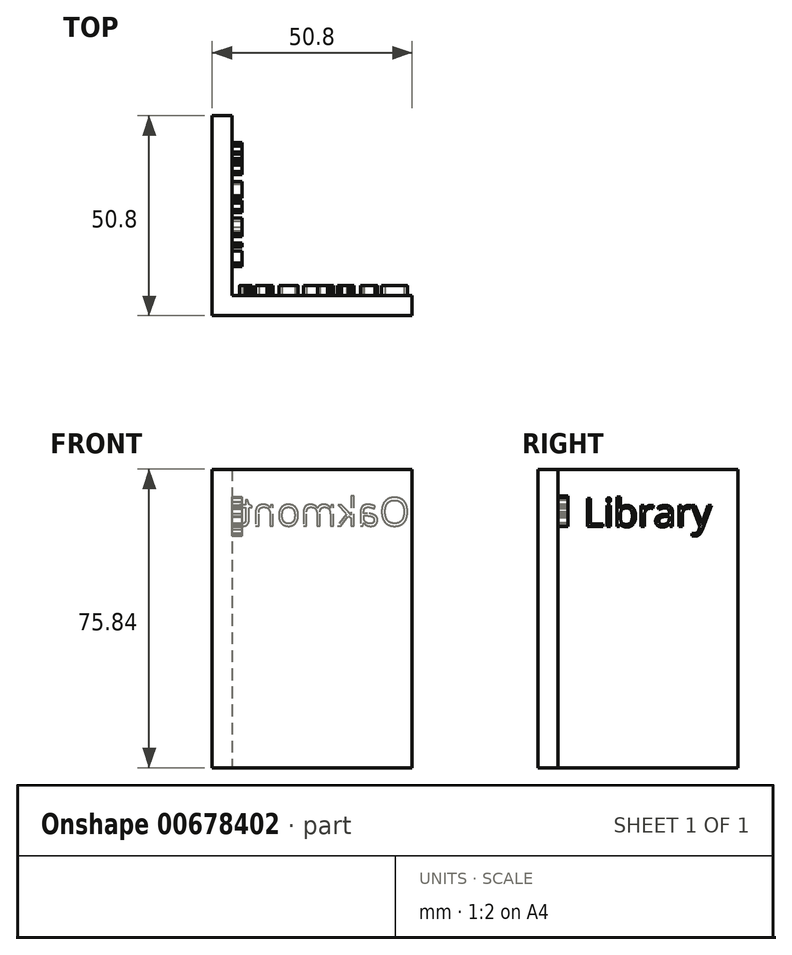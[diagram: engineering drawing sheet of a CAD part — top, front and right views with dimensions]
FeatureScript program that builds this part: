
annotation { "Feature Type Name" : "Feature", "Feature Type Description" : "" }
export const myFeature = defineFeature(function(context is Context, id is Id, definition is map)
    precondition{}
    {
        {
            var Q0;
            Q0=qCreatedBy(makeId("Right.planeOp"),FACE);
            var sketch = newSketch(context, id + "F0", { "sketchPlane" : qUnion([Q0])});
            skLineSegment(sketch, "E0.bottom", {"start": v(25.4, 37.92) * mm, "end": v(-25.4, 37.92) * mm});
            skLineSegment(sketch, "E0.top", {"start": v(25.4, -37.92) * mm, "end": v(-25.4, -37.92) * mm});
            skLineSegment(sketch, "E0.left", {"start": v(25.4, 37.92) * mm, "end": v(25.4, -37.92) * mm});
            skLineSegment(sketch, "E0.right", {"start": v(-25.4, 37.92) * mm, "end": v(-25.4, -37.92) * mm});
            skPoint(sketch, "E0.middle", {"position": v(0, 0) * mm});
            skSolve(sketch);
        }
        {
            var Q0;
            Q0 = qSketchRegion(id + "F0", true);
            extrude(context, id + "F1", {"entities" : qUnion([Q0]), "depth" : 5.08 * mm, "offsetDistance" : 25.4 * mm});
        }
        {
            var Q0;
            Q0=makeQuery(id+"F1.opExtrude","CAP_FACE",FACE,{"disambiguationData":[OSD([sQuery(id+"F0.wireOp",EDGE,"E0.bottom"),sQuery(id+"F0.wireOp",EDGE,"E0.top"),sQuery(id+"F0.wireOp",EDGE,"E0.left"),sQuery(id+"F0.wireOp",EDGE,"E0.right")])],"isStart":false});
            var sketch = newSketch(context, id + "F2", { "sketchPlane" : qUnion([Q0])});
            skLineSegment(sketch, "E1", {"start": v(-25.4, 37.92) * mm, "end": v(-20.32, 37.92) * mm});
            skLineSegment(sketch, "E2", {"start": v(-20.32, -37.92) * mm, "end": v(-25.4, -37.92) * mm});
            skLineSegment(sketch, "E3", {"start": v(-20.32, 37.92) * mm, "end": v(-20.32, -37.92) * mm});
            skSolve(sketch);
        }
        {
            var Q0;
            Q0=makeQuery(id+"F2.imprint","IMPRINT",FACE,{"disambiguationData":[TD([[makeQuery(id+"F2.imprint","IMPRINT",EDGE,{"derivedFrom":sQuery(id+"F2.wireOp",EDGE,"E1")}),1.0]])]});
            extrude(context, id + "F3", {"entities" : qUnion([Q0]), "operationType" : NewBodyOperationType.ADD, "depth" : 45.72 * mm, "offsetDistance" : 25.4 * mm});
        }
        {
            var Q0;
            Q0=makeQuery(id+"F3.opExtrude","SWEPT_FACE",FACE,{"disambiguationData":[OSD([sQuery(id+"F2.wireOp",EDGE,"E3")])]});
            var sketch = newSketch(context, id + "F4", { "sketchPlane" : qUnion([Q0])});
            skText(sketch, "E4", { "text": "Oakmont", "fontName": "OpenSans-Regular.ttf"});
            const initialGuessF4  = {"E4": [-0.05022, 0.02353, 1, 0, 0.00718]};
            skSetInitialGuess(sketch, initialGuessF4);
            skSolve(sketch);
        }
        {
            var Q0;
            Q0=makeQuery(id+"F1.opExtrude","CAP_FACE",FACE,{"disambiguationData":[OSD([sQuery(id+"F0.wireOp",EDGE,"E0.bottom"),sQuery(id+"F0.wireOp",EDGE,"E0.top"),sQuery(id+"F0.wireOp",EDGE,"E0.left"),sQuery(id+"F0.wireOp",EDGE,"E0.right")])],"isStart":false});
            var sketch = newSketch(context, id + "F5", { "sketchPlane" : qUnion([Q0])});
            skText(sketch, "E5", { "text": "Library", "fontName": "OpenSans-Regular.ttf"});
            const initialGuessF5  = {"E5": [-0.01388, 0.02332, 1, 0, 0.00718]};
            skSetInitialGuess(sketch, initialGuessF5);
            skSolve(sketch);
        }
        {
            var Q0;
            Q0 = qSketchRegion(id + "F4", true);
            extrude(context, id + "F6", {"entities" : qUnion([Q0]), "operationType" : NewBodyOperationType.ADD, "depth" : 2.54 * mm, "offsetDistance" : 25.4 * mm});
        }
        {
            var Q0;
            Q0 = qSketchRegion(id + "F5", true);
            extrude(context, id + "F7", {"entities" : qUnion([Q0]), "operationType" : NewBodyOperationType.ADD, "depth" : 2.54 * mm, "offsetDistance" : 25.4 * mm});
        }
    });
